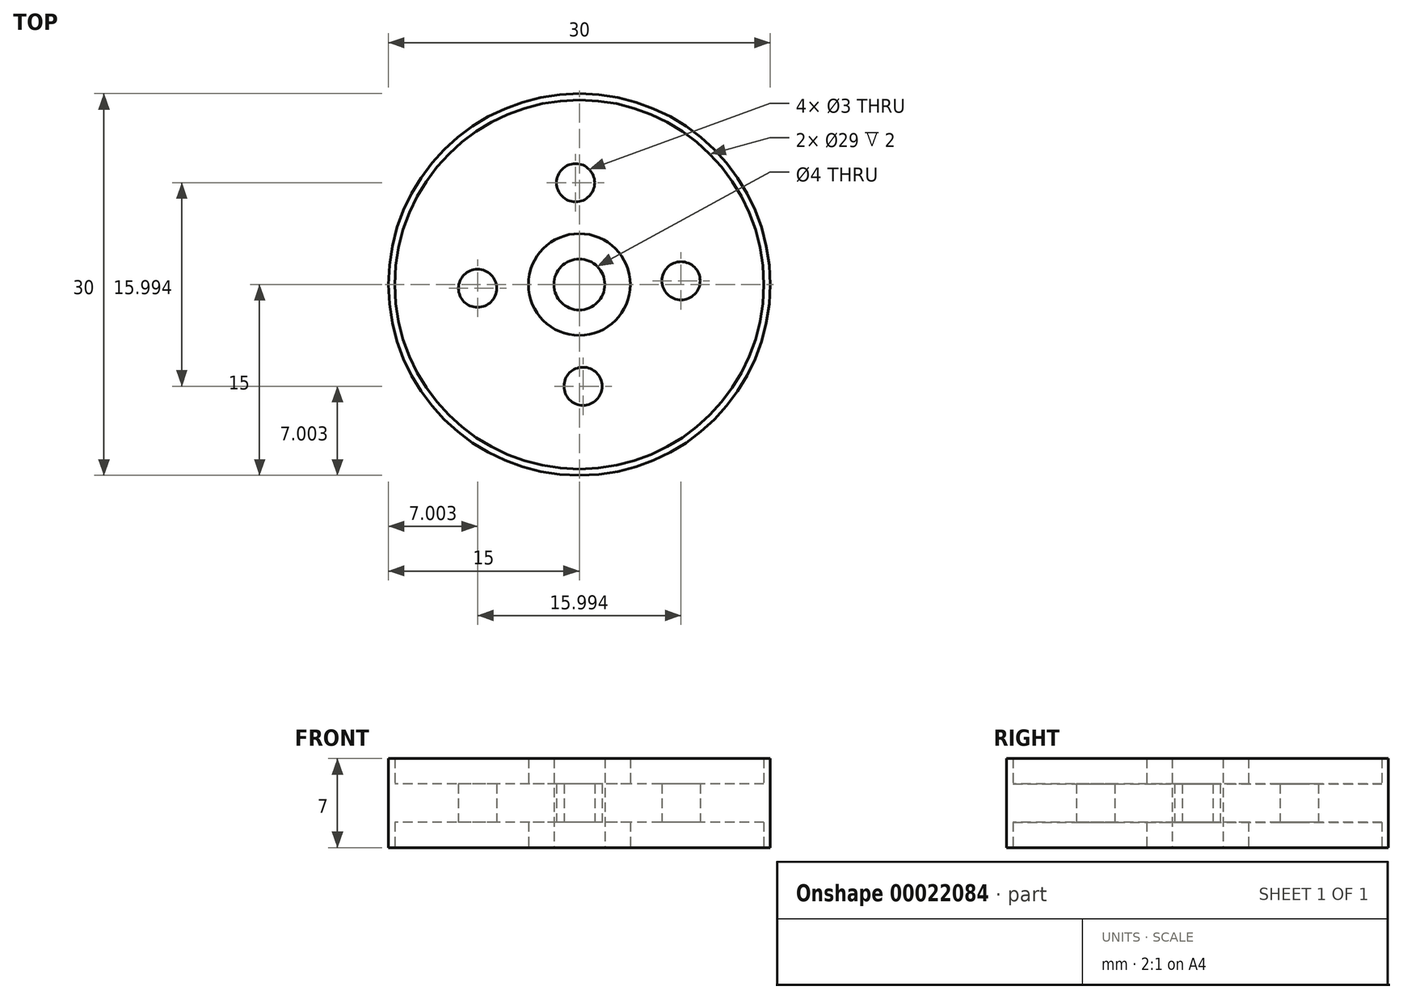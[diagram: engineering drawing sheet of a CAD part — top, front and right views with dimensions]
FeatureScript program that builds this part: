
annotation { "Feature Type Name" : "Feature", "Feature Type Description" : "" }
export const myFeature = defineFeature(function(context is Context, id is Id, definition is map)
    precondition{}
    {
        {
            var Q0;
            Q0=qCreatedBy(makeId("Top.planeOp"),FACE);
            var sketch = newSketch(context, id + "F0", { "sketchPlane" : qUnion([Q0])});
            skLineSegment(sketch, "E0", {"start": v(15, 0) * mm, "end": v(15.21, 0) * mm});
            skCircle(sketch, "E1", {"center": v(0, 0) * mm, "radius": 15 * mm});
            skPoint(sketch, "E2.orphan", {"position": v(-15, 0) * mm});
            skCircle(sketch, "E3", {"center": v(0, 0) * mm, "radius": 14.5 * mm});
            skCircle(sketch, "E4", {"center": v(0, 0) * mm, "radius": 4 * mm});
            skCircle(sketch, "E5", {"center": v(0, 0) * mm, "radius": 2 * mm});
            skCircle(sketch, "E6", {"center": v(-0.3, 8) * mm, "radius": 1.5 * mm});
            skLineSegment(sketch, "E7.trimOffspring", {"start": v(-0.3, 14.5) * mm, "end": v(-0.3, 15) * mm});
            skCircle(sketch, "E8.1.0", {"center": v(-8, -0.3) * mm, "radius": 1.5 * mm});
            skCircle(sketch, "E8.2.0", {"center": v(0.3, -8) * mm, "radius": 1.5 * mm});
            skCircle(sketch, "E8.3.0", {"center": v(8, 0.3) * mm, "radius": 1.5 * mm});
            skSolve(sketch);
        }
        {
            var Q0;
            Q0=makeQuery(id+"F0.imprint","IMPRINT",FACE,{"disambiguationData":[TD([[makeQuery(id+"F0.imprint","IMPRINT",EDGE,{"derivedFrom":sQuery(id+"F0.wireOp",EDGE,"E3")}),-1.0]])]});
            extrude(context, id + "F1", {"entities" : qUnion([Q0]), "endBound" : BoundingType.SYMMETRIC, "depth" : 7 * mm});
        }
        {
            var Q0;
            Q0=makeQuery(id+"F0.imprint","IMPRINT",FACE,{"disambiguationData":[TD([[makeQuery(id+"F0.imprint","IMPRINT",EDGE,{"derivedFrom":sQuery(id+"F0.wireOp",EDGE,"E3")}),1.0]])]});
            extrude(context, id + "F2", {"entities" : qUnion([Q0]), "operationType" : NewBodyOperationType.ADD, "endBound" : BoundingType.SYMMETRIC, "depth" : 3 * mm});
        }
        {
            var Q0;
            Q0=makeQuery(id+"F0.imprint","IMPRINT",FACE,{"disambiguationData":[TD([[makeQuery(id+"F0.imprint","IMPRINT",EDGE,{"derivedFrom":sQuery(id+"F0.wireOp",EDGE,"E4")}),1.0]])]});
            extrude(context, id + "F3", {"entities" : qUnion([Q0]), "operationType" : NewBodyOperationType.ADD, "endBound" : BoundingType.SYMMETRIC, "depth" : 7 * mm});
        }
    });
